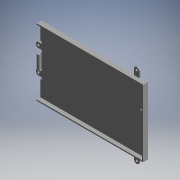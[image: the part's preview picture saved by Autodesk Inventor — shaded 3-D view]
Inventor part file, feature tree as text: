
AUTODESK INVENTOR PART (.ipt)
format: ipt  version: 2019 (Build 230136000, 136)  size: 189,952 bytes
history: native  units: mm (DEFAULTED — no unit token found)
features: extrude x4, sketch x3, projected_geometry x3, chamfer x2
ambient origin geometry x8: Origin, YZ Plane, XZ Plane, XY Plane, X Axis, Y Axis, Z Axis, Center Point
bodies: Solid1 (feature_tree)
feature tree (12):
  sketch  "Sketch1"  dims[d8=3.0mm d9=4.5mm]
  extrude  "Extrusion1"  Depth=4.5mm
  extrude  "Extrusion2"  Depth=1.6mm
  extrude  "Extrusion3"  Depth=7.5mm
  chamfer  "Chamfer1"  Distance=112.2mm
  extrude  "Extrusion4"  Depth=1.6mm
  chamfer  "Chamfer2"  Distance=22.5mm
  sketch  "Sketch2"  dims[d11=1.6mm d14=3.0mm]
  projected_geometry  "Projected Loop1"
  projected_geometry  "Projected Loop2"
  sketch  "Sketch3"  dims[d15=7.5mm d17=7.5mm d19=112.2mm d23=1.6mm d27=22.5mm d28=1.6mm d29=1.6mm d30=148.5mm d31=92.5mm d32=1.6mm d34=140.0mm d36=33.75mm d37=7.5mm d38=1.6mm d39=0.0mm d40=7.0mm d41=0.0mm d42=2.0mm d43=30.0mm d44=3.5mm d45=0.0mm d46=2.0mm d47=2.0mm d48=45.0deg d49=2.2mm d50=2.0mm d51=0.0mm d52=0.75mm d53=2.0mm d54=45.0deg]
  projected_geometry  "Projected Loop3"
